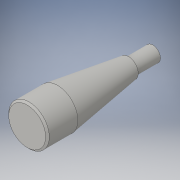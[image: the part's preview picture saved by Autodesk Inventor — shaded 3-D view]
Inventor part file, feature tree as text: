
AUTODESK INVENTOR PART (.ipt)
format: ipt  version: 2016 (Build 200138000, 138)  size: 118,272 bytes
history: native  units: in
note: dims shown in document units (in); Inventor stores cm internally (conversion verified against a paired STEP export)
features: sketch x4, extrude x3, loft x1, chamfer x1, other x1
ambient origin geometry x8: Origin, YZ Plane, XZ Plane, XY Plane, X Axis, Y Axis, Z Axis, Center Point
bodies: Solid1 (feature_tree)
feature tree (10):
  extrude  "Extrusion1"  Depth=0.6in TaperAngle=0.0deg
  extrude  "Extrusion2"  Depth=1.75in TaperAngle=0.0deg
  loft  "Loft1"
  extrude  "Extrusion3"  Depth=0.75in TaperAngle=0.0deg
  chamfer  "Chamfer1"  Distance=0.045in Angle=45.0deg
  sketch  "Sketch1"  dims[d0=0.375in d1=0.6in d2=0.0in]
  sketch  "Sketch2"  dims[d3=0.48in d5=1.75in d6=0.0in]
  sketch  "Sketch3"  dims[d7=1.0in d8=0.0in d9=90.0deg]
  other  "Edges1"
  sketch  "Sketch4"  dims[d10=0.0in d11=90.0deg d12=0.75in d13=0.0in d14=0.045in d15=0.125in d16=45.0deg]
